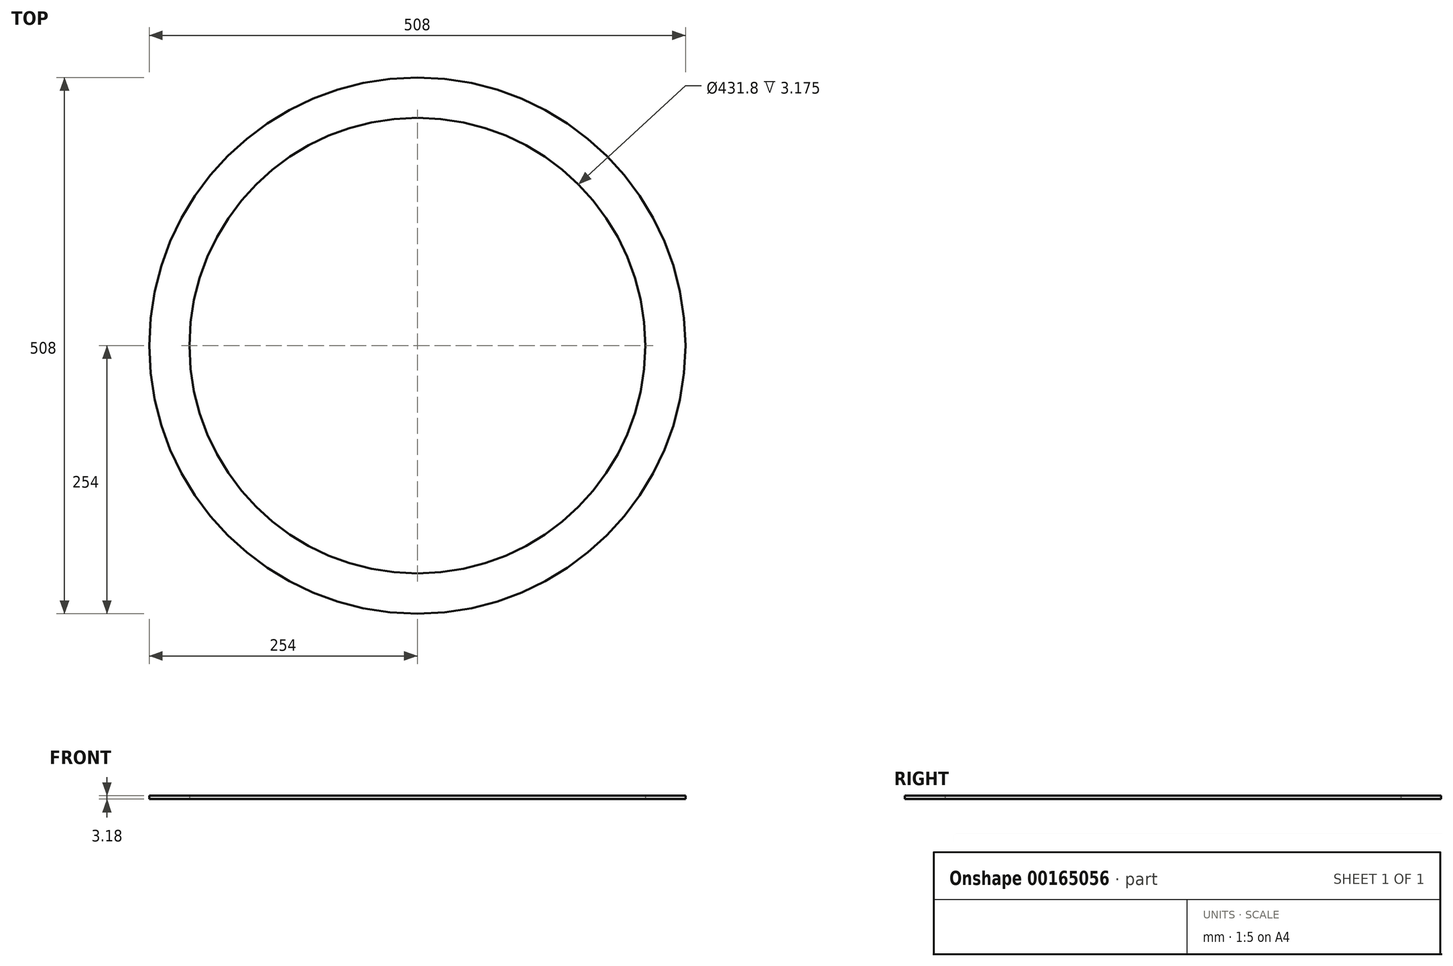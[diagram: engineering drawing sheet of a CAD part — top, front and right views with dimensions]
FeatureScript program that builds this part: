
annotation { "Feature Type Name" : "Feature", "Feature Type Description" : "" }
export const myFeature = defineFeature(function(context is Context, id is Id, definition is map)
    precondition{}
    {
        {
            var Q0;
            Q0=qCreatedBy(makeId("Top.planeOp"),FACE);
            var sketch = newSketch(context, id + "F0", { "sketchPlane" : qUnion([Q0])});
            skCircle(sketch, "E0", {"center": v(0, 0) * mm, "radius": 215.9 * mm});
            skCircle(sketch, "E1", {"center": v(0, 0) * mm, "radius": 254 * mm});
            skSolve(sketch);
        }
        {
            var Q0;
            Q0=qSketchRegion(id+"F0",true);
            extrude(context, id + "F1", {"entities" : qUnion([Q0]), "depth" : 3.17 * mm});
        }
    });
